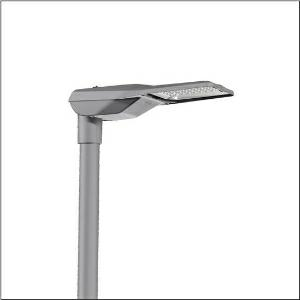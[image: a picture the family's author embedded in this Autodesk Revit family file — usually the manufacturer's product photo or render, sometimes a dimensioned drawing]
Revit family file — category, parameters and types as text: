
# Revit family: streetlight_sl_21_mini___p1_0a_5xe2a33s08gb_ad59
name_source: partatom
category: Lighting Fixtures
units: mm (PartAtom-declared; Revit-internal decimal feet)

## family parameters
Cut with Voids When Loaded = No
Host = Face
Light Source = No
Part Type = Normal
Room Calculation Point = No
Round Connector Dimension = Use Diameter
Shared = No

## types (1)
- --- (1 x LED, 5940 lm, 40.4 W, 3000K)
    Apparent Load = 40 VA
    CIE Flux Codes = 21 50 90 100 100
    Color Rendering = 70
    Color Temperature = 3000K
    Default Elevation = 1800 mm
    Description = Streetlight SL 21 mini, mast luminaire, primary light control with lens, of PMMA, primary optical cover: cover, of toughened safety glass, transparent, light distribution: P1.0a, light emission: direct distribution, primary light characteristic: asymmetric, installation type: side-entry, post-top, LED, High Power LED, rated luminous flux: 5.940lm, luminous efficacy: 147lm/W, light colour: 730, colour temperature: 3000K, control gear: D4i, control: overheat protection, constant luminous flux control, time-dependent luminous flux control, flexible luminous flux parameterisation, pre-setting: logarithmic dimming characteristic, mains connection: 220..240V, AC, 50/60Hz, start of lifetime: 40W, end of service life: 41W, reduction: 19W, luminaire housing, of diecast aluminium, powder-coated, SITECO metallic grey (DB 702S), corrosivity category C5 high according to DIN EN ISO 12944, please order mast flange separately, inclination adjustable: 0°, 5°, 10°, 15°, sealing non-destructively replaceable, multi-level sealing system, length: 628mm, width: 235mm, height: 110mm, mast flange for spigot size: 42mm (side-entry): 5XC10008XM4, 60/48mm (side-entry/post-top): 5XC10108XM2, 76/60mm (side-entry/post-top): 5XC10108XM1, mounting height: 4..8m, Smart Interface above, protection rating (complete): IP66, insulation class (complete): insulation class II (safety insulation), certification: CE, ENEC, ENEC+, VDE, impact resistance: IK10, permissible operating ambient temperature for outdoor applications: -40..+50°C, standard-compliant lighting for roads and squares, packaging unit: 1 piece

Light Distribution: P1.0a
    Height = 110 mm
    Lamp = 1 x LED
    Lamp Light Flux = 5940 lm
    Lamp Power = 40.4 W
    Lamp count = 1
    Length = 625 mm
    Luminous efficacy = 147 lm/W
    Manufacturer = Siteco
    ModVariant = No
    Model = 5XE2A33S08GB
    Number of Poles = 1
    OnlyDefault = Yes
    Power Factor = 1
    Product Name = Streetlight SL 21 mini | P1.0a
    Product group = mast luminaire | pylon top
    ProductGroupID = 6100
    Protection Class = Protection class II
    Protection Degree = IP 66
    RLX_Detail_Level = 1
    RLX_Emergency_Light_Flux = 0 lm
    RLX_Emergency_Type = 0
    RLX_Emergency_Type_DB = No
    RlxData = <blob elided: 37341 chars, md5=1f3187af>
    Socket = socket
    Standby Power = 0 W
    System Light Flux = 5940 lm
    System Power = 40 W
    Type Comments = factory setting: luminous flux: 100 % | dim-lin: 254 | 812 mA
    Type Image = l_1003515.jpg
    URL = http://relux.com
    VarID = @adj_184165
    Voltage = 0 V
    Weight = 0.00 kg
    Width = 234 mm

## geometry (parser evidence)
native form markers: Blend x4, Sweep x10
no freeform markers — native parametric forms only
